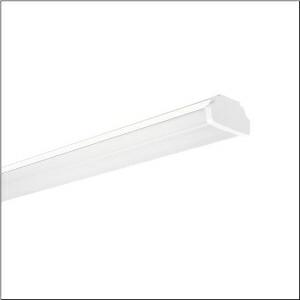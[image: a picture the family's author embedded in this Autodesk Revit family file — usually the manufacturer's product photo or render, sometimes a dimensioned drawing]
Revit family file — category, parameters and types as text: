
# Revit family: modario_r__31_gen_2_53bm812cv6a5d2_682d
name_source: partatom
category: Lighting Fixtures
units: mm (PartAtom-declared; Revit-internal decimal feet)

## family parameters
Cut with Voids When Loaded = No
Host = Face
Light Source = No
Part Type = Normal
Room Calculation Point = No
Round Connector Dimension = Use Diameter
Shared = No

## types (1)
- --- (1 x LED, 10550 lm, 56.5 W, 6500K)
    Apparent Load = 57 VA
    CIE Flux Codes = 47 80 95 93 100
    Color Rendering = 80
    Color Temperature = 6500K
    Default Elevation = 1800 mm
    Description = Modario® 31 Gen.2, luminaire insert, of sheet steel, coil coated, white, length: 1.495mm, width: 81mm, height: 82mm, 5x system unit, system units: 299mm, LED rated luminous flux: 10.550lm, light colour: 865, control gear: ON/OFF Multilumen, CLOi, with plug, 3-pole, with phase selection, mains connection: 220..240V, AC, 50/60Hz, start of lifetime: 57W, end of service life: 68W, through-wiring accessed according to module size, primary optical cover: cover, of PMMA, light emission: direct distribution, primary light characteristic: symmetric, protection rating (complete): IP20, protection rating (LED compartment): IP50, insulation class (complete): insulation class I (protective earthing), certification: CE, ENEC, VDE, UKCA, impact resistance: IK03, permissible ambient temperature for indoor applications: -35..+40°C, corresponds to IFS (International Featured Standards) requirements for safety and quality in the food industry, reducing of maximum allowable ambient temperature of 5°C with ceiling mounting, IP40 when using the optional accessory 5TP9018, packaging unit: 1 piece
    Height = 92 mm
    Lamp = 1 x LED
    Lamp Light Flux = 10550 lm
    Lamp Power = 56.5 W
    Lamp count = 1
    Length = 1495 mm
    Luminous efficacy = 187 lm/W
    Manufacturer = Siteco
    ModVariant = No
    Model = 53BM812CV6A5D2
    Mounting Place = Ceiling
    Mounting Type = Pendant
    Number of Poles = 1
    OnlyDefault = Yes
    Power Factor = 1
    Product Name = Modario® 31 Gen.2
    Product group = luminaire insert
    ProductGroupID = 902
    Protection Class = Protection class I
    Protection Degree = IP 20
    RLX_Detail_Level = 1
    RLX_Emergency_Light_Flux = 0 lm
    RLX_Emergency_Type = 0
    RLX_Emergency_Type_DB = No
    RlxData = <blob elided: 40025 chars, md5=6c5f4c6d>
    Socket = socket
    Standby Power = 0 W
    System Light Flux = 10550 lm
    System Power = 57 W
    Type Comments = factory setting: luminous flux: 100 % | (A | C | E) | 133 mA
    Type Image = l_1341886.jpg
    URL = http://relux.com
    VarID = @adj_034082
    Voltage = 0 V
    Weight = 0.00 kg
    Width = 81 mm

## geometry (parser evidence)
native form markers: Blend x4, Sweep x12
no freeform markers — native parametric forms only
